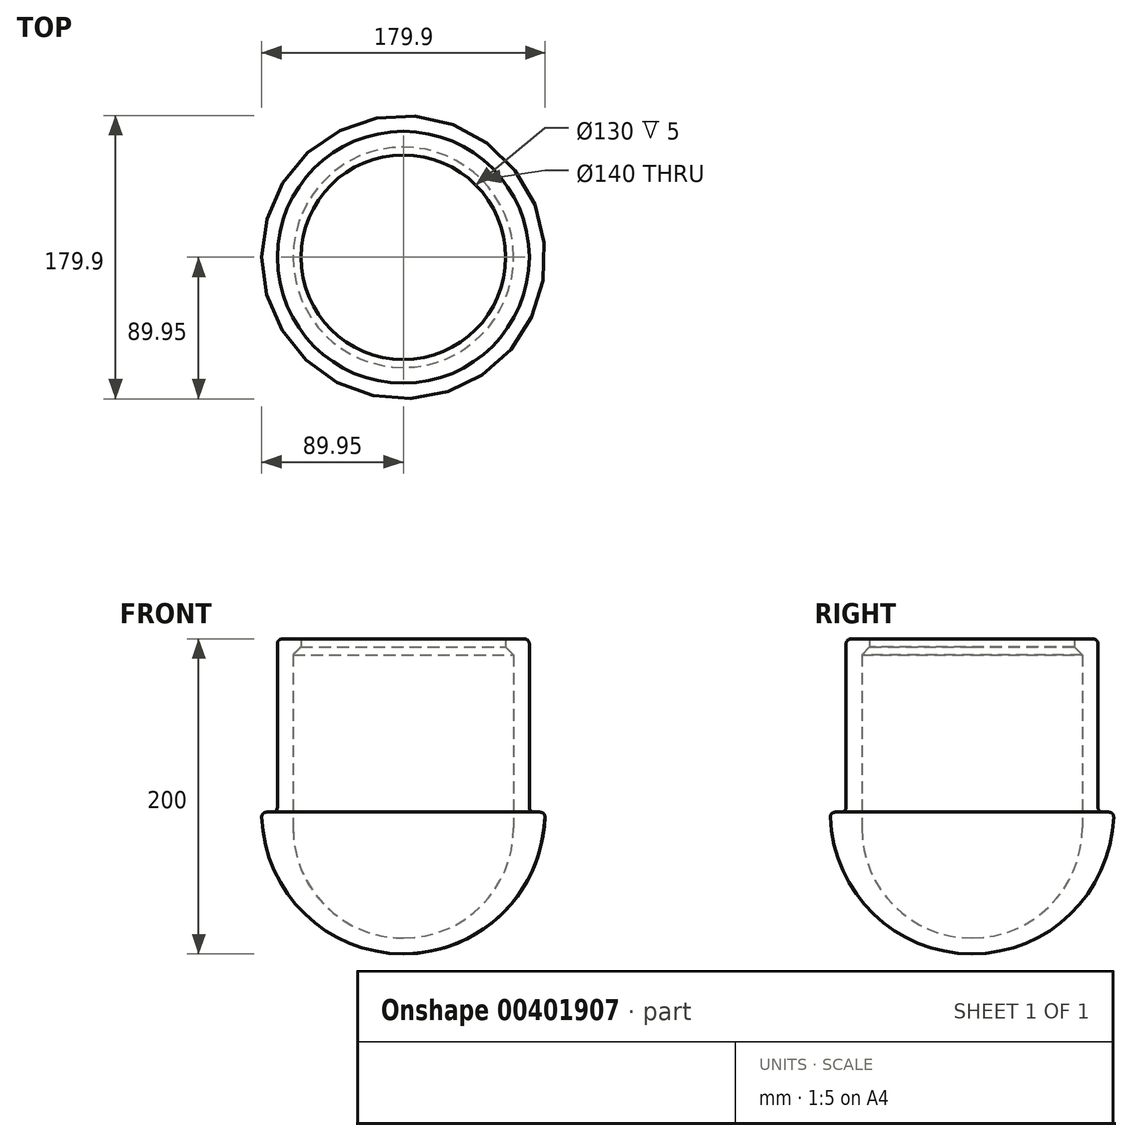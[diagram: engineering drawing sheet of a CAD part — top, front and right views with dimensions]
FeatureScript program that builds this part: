
annotation { "Feature Type Name" : "Feature", "Feature Type Description" : "" }
export const myFeature = defineFeature(function(context is Context, id is Id, definition is map)
    precondition{}
    {
        {
            var Q0;
            Q0=qCreatedBy(makeId("Front.planeOp"),FACE);
            var sketch = newSketch(context, id + "F0", { "sketchPlane" : qUnion([Q0])});
            skLineSegment(sketch, "E0", {"start": v(80, 0) * mm, "end": v(80, 110) * mm});
            skLineSegment(sketch, "E1", {"start": v(80, 110) * mm, "end": v(65, 110) * mm});
            skLineSegment(sketch, "E2", {"start": v(65, 110) * mm, "end": v(65, 100) * mm});
            skLineSegment(sketch, "E3", {"start": v(65, 100) * mm, "end": v(70, 100) * mm});
            skLineSegment(sketch, "E4", {"start": v(70, 100) * mm, "end": v(70, -10) * mm});
            skArc(sketch, "E5", {"start": v(0, -90) * mm, "mid": v(63.64, -63.64) * mm, "end": v(90, 0) * mm});
            skLineSegment(sketch, "E6", {"start": v(80, 0) * mm, "end": v(90, 0) * mm});
            skLineSegment(sketch, "E7", {"start": v(0, -90) * mm, "end": v(0, -80) * mm});
            skArc(sketch, "E8", {"start": v(0, -80) * mm, "mid": v(49.5, -59.5) * mm, "end": v(70, -10) * mm});
            skLineSegment(sketch, "E9", {"start": v(0, -80) * mm, "end": v(0, -75) * mm});
            skLineSegment(sketch, "E10", {"start": v(70, 0) * mm, "end": v(65, 0) * mm});
            skArc(sketch, "E11", {"start": v(0, -75) * mm, "mid": v(46.27, -49.44) * mm, "end": v(65, 0) * mm});
            skSolve(sketch);
        }
        {
            var Q0;
            Q0=makeQuery(id+"F0.imprint","IMPRINT",FACE,{"disambiguationData":[TD([[makeQuery(id+"F0.imprint","IMPRINT",EDGE,{"derivedFrom":sQuery(id+"F0.wireOp",EDGE,"E0")}),1.0]])]});
            var Q1;
            Q1=sQuery(id+"F0.wireOp",EDGE,"E7");
            revolve(context, id + "F1", {"entities" : qUnion([Q0]), "axis" : qUnion([Q1]), "revolveType" : RevolveType.FULL});
        }
        {
            var Q0;
            Q0=makeQuery(id+"F1.opRevolve","SWEPT_EDGE",EDGE,{"disambiguationData":[OSD([sQuery(id+"F0.wireOp",EDGE,"E5"),sQuery(id+"F0.wireOp",EDGE,"E6")])]});
            var Q1;
            Q1=makeQuery(id+"F1.opRevolve","SWEPT_EDGE",EDGE,{"disambiguationData":[OSD([sQuery(id+"F0.wireOp",EDGE,"E0"),sQuery(id+"F0.wireOp",EDGE,"E6")])]});
            var Q2;
            Q2=makeQuery(id+"F1.opRevolve","SWEPT_EDGE",EDGE,{"disambiguationData":[OSD([sQuery(id+"F0.wireOp",EDGE,"E0"),sQuery(id+"F0.wireOp",EDGE,"E1")])]});
            fillet(context, id + "F2", {"entities" : qUnion([Q0, Q1, Q2]), "radius" : 3 * mm, "tangentPropagation" : true, "allowEdgeOverflow" : false});
        }
        {
            var Q0;
            Q0=makeQuery(id+"F1.opRevolve","SWEPT_EDGE",EDGE,{"disambiguationData":[OSD([sQuery(id+"F0.wireOp",EDGE,"E2"),sQuery(id+"F0.wireOp",EDGE,"E3")])]});
            chamfer(context, id + "F3", {"entities" : qUnion([Q0]), "width" : 5 * mm, "tangentPropagation" : true});
        }
    });
